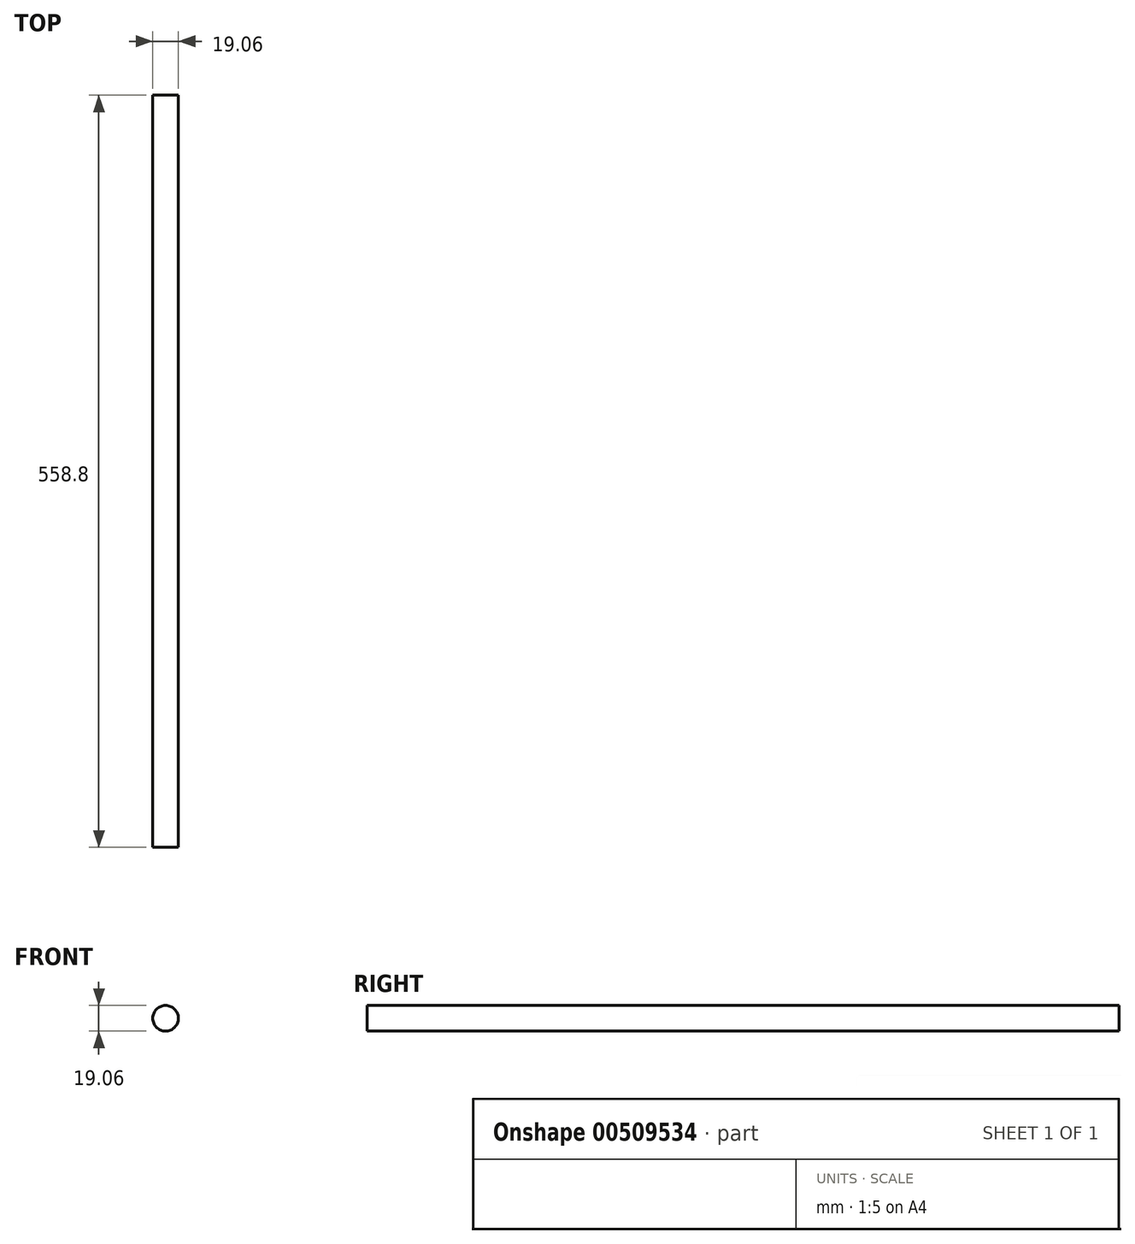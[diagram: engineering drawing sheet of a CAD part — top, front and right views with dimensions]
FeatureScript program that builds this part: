
annotation { "Feature Type Name" : "Feature", "Feature Type Description" : "" }
export const myFeature = defineFeature(function(context is Context, id is Id, definition is map)
    precondition{}
    {
        {
            var Q0;
            Q0=qCreatedBy(makeId("Top.planeOp"),FACE);
            var sketch = newSketch(context, id + "F0", { "sketchPlane" : qUnion([Q0])});
            skLineSegment(sketch, "E0.bottom", {"start": v(9.52, 279.4) * mm, "end": v(-9.52, 279.4) * mm});
            skLineSegment(sketch, "E0.top", {"start": v(9.52, -279.4) * mm, "end": v(-9.53, -279.4) * mm});
            skLineSegment(sketch, "E0.left", {"start": v(9.53, 279.4) * mm, "end": v(9.52, -279.4) * mm});
            skLineSegment(sketch, "E0.right", {"start": v(-9.52, 279.4) * mm, "end": v(-9.53, -279.4) * mm});
            skPoint(sketch, "E0.middle", {"position": v(0, 0) * mm});
            skLineSegment(sketch, "E1", {"start": v(0, -279.4) * mm, "end": v(0, 279.4) * mm});
            skSolve(sketch);
        }
        {
            var Q0;
            {var subQ0=sQuery(id+"F0.wireOp",EDGE,"E0.right");Q0=makeQuery(id+"F0.imprint","IMPRINT",FACE,{"disambiguationData":[TD([[makeQuery(id+"F0.imprint","IMPRINT",EDGE,{"derivedFrom":subQ0}),1.0]])]});}
            var Q1;
            Q1=sQuery(id+"F0.wireOp",EDGE,"E1");
            revolve(context, id + "F1", {"entities" : qUnion([Q0]), "axis" : qUnion([Q1]), "revolveType" : RevolveType.FULL});
        }
    });
